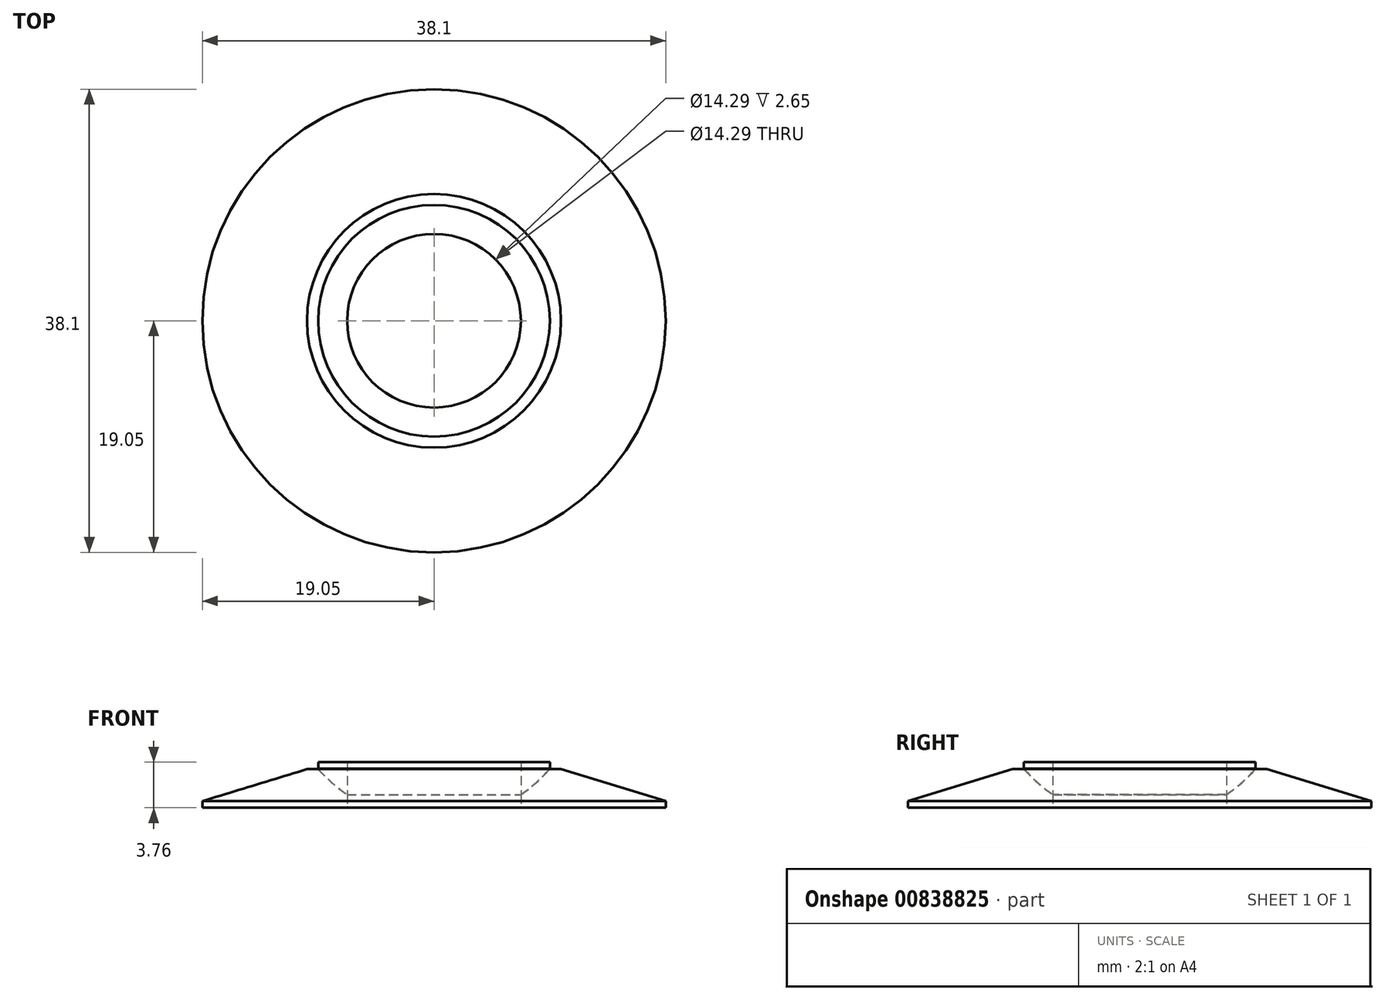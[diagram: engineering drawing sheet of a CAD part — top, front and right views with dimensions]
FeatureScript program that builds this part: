
annotation { "Feature Type Name" : "Feature", "Feature Type Description" : "" }
export const myFeature = defineFeature(function(context is Context, id is Id, definition is map)
    precondition{}
    {
        {
            var Q0;
            Q0=qCreatedBy(makeId("Front.planeOp"),FACE);
            var sketch = newSketch(context, id + "F0", { "sketchPlane" : qUnion([Q0])});
            skLineSegment(sketch, "E0", {"start": v(0, 0) * mm, "end": v(5.23, 0) * mm, "construction": true});
            skLineSegment(sketch, "E1", {"start": v(19.05, 0) * mm, "end": v(19.05, 0.54) * mm});
            skLineSegment(sketch, "E2", {"start": v(19.05, 0.54) * mm, "end": v(10.44, 3.18) * mm});
            skLineSegment(sketch, "E3", {"start": v(10.44, 3.18) * mm, "end": v(9.53, 3.18) * mm});
            skLineSegment(sketch, "E4", {"start": v(7.14, 1.07) * mm, "end": v(7.14, 0) * mm});
            skArc(sketch, "E5.trimOffspring", {"start": v(7.14, 1.07) * mm, "mid": v(8.4, 2.05) * mm, "end": v(9.52, 3.18) * mm});
            skLineSegment(sketch, "E6.trimOffspring", {"start": v(7.14, 0) * mm, "end": v(19.05, 0) * mm});
            skLineSegment(sketch, "E7", {"start": v(0, 0) * mm, "end": v(0, 2.37) * mm, "construction": true});
            skSolve(sketch);
        }
        {
            var Q0;
            Q0=makeQuery(id+"F0.imprint","IMPRINT",FACE,{"disambiguationData":[TD([[makeQuery(id+"F0.imprint","IMPRINT",EDGE,{"derivedFrom":sQuery(id+"F0.wireOp",EDGE,"E1")}),1.0]])]});
            var Q1;
            Q1=sQuery(id+"F0.wireOp",EDGE,"E7");
            revolve(context, id + "F1", {"surfaceOperationType" : NewSurfaceOperationType.NEW, "entities" : qUnion([Q0]), "axis" : qUnion([Q1]), "revolveType" : RevolveType.FULL});
        }
        {
            var Q0;
            Q0=qCreatedBy(makeId("Front.planeOp"),FACE);
            var sketch = newSketch(context, id + "F2", { "sketchPlane" : qUnion([Q0])});
            skArc(sketch, "E8.0", {"start": v(7.14, 1.1) * mm, "mid": v(8.4, 2.08) * mm, "end": v(9.53, 3.21) * mm});
            skLineSegment(sketch, "E9", {"start": v(9.53, 3.21) * mm, "end": v(9.53, 3.76) * mm});
            skLineSegment(sketch, "E10", {"start": v(9.53, 3.76) * mm, "end": v(7.14, 3.76) * mm});
            skLineSegment(sketch, "E11", {"start": v(7.14, 3.76) * mm, "end": v(7.14, 1.1) * mm});
            skSolve(sketch);
        }
        {
            var Q0;
            Q0 = qSketchRegion(id + "F2", true);
            var Q1;
            Q1=sQuery(id+"F0.wireOp",EDGE,"E7");
            revolve(context, id + "F3", {"surfaceOperationType" : NewSurfaceOperationType.NEW, "entities" : qUnion([Q0]), "axis" : qUnion([Q1]), "revolveType" : RevolveType.FULL});
        }
    });
